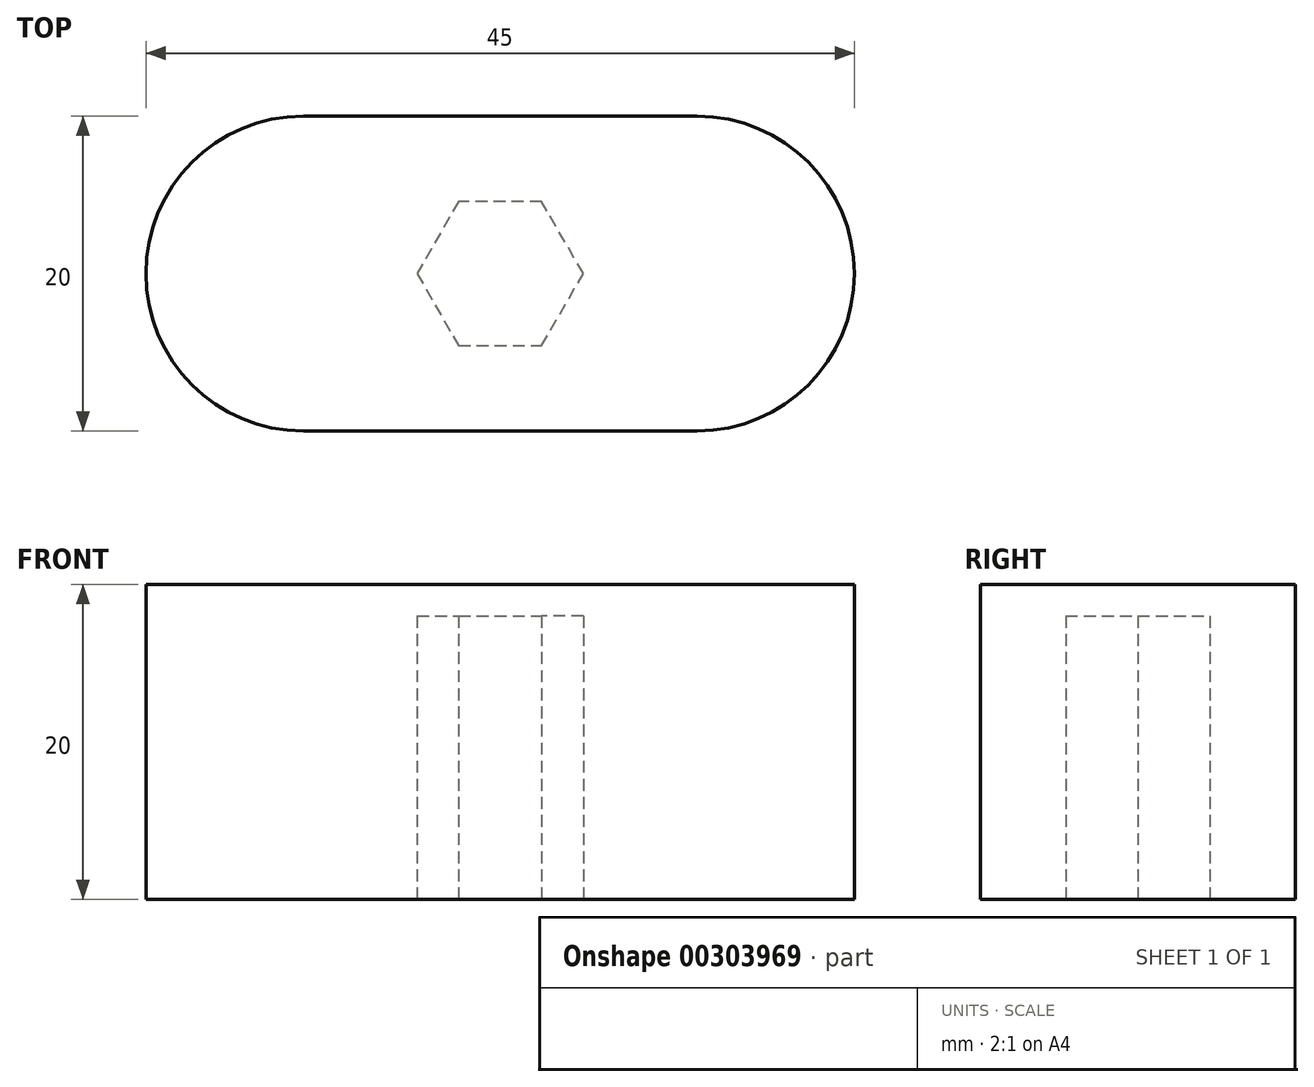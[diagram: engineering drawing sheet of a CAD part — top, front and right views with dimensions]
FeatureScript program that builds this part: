
annotation { "Feature Type Name" : "Feature", "Feature Type Description" : "" }
export const myFeature = defineFeature(function(context is Context, id is Id, definition is map)
    precondition{}
    {
        {
            var Q0;
            Q0=qCreatedBy(makeId("Top.planeOp"),FACE);
            var sketch = newSketch(context, id + "F0", { "sketchPlane" : qUnion([Q0])});
            skLineSegment(sketch, "E0.bottom", {"start": v(22.5, -10) * mm, "end": v(-22.5, -10) * mm});
            skLineSegment(sketch, "E0.top", {"start": v(22.5, 10) * mm, "end": v(-22.5, 10) * mm});
            skLineSegment(sketch, "E0.left", {"start": v(22.5, -10) * mm, "end": v(22.5, 10) * mm});
            skLineSegment(sketch, "E0.right", {"start": v(-22.5, -10) * mm, "end": v(-22.5, 10) * mm});
            skPoint(sketch, "E0.middle", {"position": v(0, 0) * mm});
            skSolve(sketch);
        }
        {
            var Q0;
            Q0 = qSketchRegion(id + "F0", true);
            extrude(context, id + "F1", {"entities" : qUnion([Q0]), "depth" : 20 * mm});
        }
        {
            var Q0;
            Q0=makeQuery(id+"F1.opExtrude","CAP_FACE",FACE,{"disambiguationData":[OSD([sQuery(id+"F0.wireOp",EDGE,"E0.bottom"),sQuery(id+"F0.wireOp",EDGE,"E0.top"),sQuery(id+"F0.wireOp",EDGE,"E0.left"),sQuery(id+"F0.wireOp",EDGE,"E0.right")])],"isStart":true});
            var sketch = newSketch(context, id + "F2", { "sketchPlane" : qUnion([Q0])});
            skCircle(sketch, "E1.cCircle", {"center": v(0, 0) * mm, "radius": 4.57 * mm, "construction": true});
            skLineSegment(sketch, "E1.0", {"start": v(5.28, 0) * mm, "end": v(2.64, -4.57) * mm});
            skLineSegment(sketch, "E1.1", {"start": v(2.64, -4.57) * mm, "end": v(-2.64, -4.57) * mm});
            skLineSegment(sketch, "E1.2", {"start": v(-2.64, -4.57) * mm, "end": v(-5.28, 0) * mm});
            skLineSegment(sketch, "E1.3", {"start": v(-5.28, 0) * mm, "end": v(-2.64, 4.57) * mm});
            skLineSegment(sketch, "E1.4", {"start": v(-2.64, 4.57) * mm, "end": v(2.64, 4.57) * mm});
            skLineSegment(sketch, "E1.5", {"start": v(2.64, 4.57) * mm, "end": v(5.28, 0) * mm});
            skPoint(sketch, "E1.0.midPoint", {"position": v(3.96, -2.29) * mm});
            skSolve(sketch);
        }
        {
            var Q0;
            Q0 = qSketchRegion(id + "F2", true);
            extrude(context, id + "F3", {"entities" : qUnion([Q0]), "operationType" : NewBodyOperationType.REMOVE, "oppositeDirection" : true, "depth" : 18 * mm});
        }
        {
            var Q0;
            Q0=makeQuery(id+"F1.opExtrude","SWEPT_EDGE",EDGE,{"disambiguationData":[OSD([sQuery(id+"F0.wireOp",EDGE,"E0.bottom"),sQuery(id+"F0.wireOp",EDGE,"E0.left")])]});
            var Q1;
            Q1=makeQuery(id+"F1.opExtrude","SWEPT_EDGE",EDGE,{"disambiguationData":[OSD([sQuery(id+"F0.wireOp",EDGE,"E0.bottom"),sQuery(id+"F0.wireOp",EDGE,"E0.right")])]});
            var Q2;
            Q2=makeQuery(id+"F1.opExtrude","SWEPT_EDGE",EDGE,{"disambiguationData":[OSD([sQuery(id+"F0.wireOp",EDGE,"E0.top"),sQuery(id+"F0.wireOp",EDGE,"E0.left")])]});
            var Q3;
            Q3=makeQuery(id+"F1.opExtrude","SWEPT_EDGE",EDGE,{"disambiguationData":[OSD([sQuery(id+"F0.wireOp",EDGE,"E0.top"),sQuery(id+"F0.wireOp",EDGE,"E0.right")])]});
            fillet(context, id + "F4", {"entities" : qUnion([Q0, Q1, Q2, Q3]), "radius" : 10 * mm, "tangentPropagation" : true, "allowEdgeOverflow" : false});
        }
    });
